# Revit family: Spec Equip_Shelf_Shower_Argent_Mondrian Neu_800mm
name_source: partatom
category: Specialty Equipment
revit_build: Autodesk Revit 2016 (Build: 20190508_0715(x64)
units: mm (PartAtom-declared; Revit-internal decimal feet)

## family parameters
Always vertical = Yes
Cut with Voids When Loaded = Yes
OmniClass Number = 23.40.20.21
OmniClass Title = Toilet and Bath Specialties
Part Type = Normal
Room Calculation Point = No
Round Connector Dimension = Use Diameter
Shared = No
Work Plane-Based = No

## types (1)
- Chrome (AR93611D)
    Body Material = z_Argent_Chrome
    CW Connection = No
    CWFU = 0
    Cost = 0 $
    Description = Mondrian Neu 300 Shower Shelf
    HW Connection = No
    HWFU = 0
    IfcExportAs = IfcSanitaryTerminalType
    IfcExportType = SHELF
    Manufacturer = Argent
    Manufacturer_Overall Depth = 100 mm
    Manufacturer_Overall Height = 25 mm
    Manufacturer_Overall Width = 300 mm
    Manufacturer_Spec Code = AR93611D
    Manufacturer_URL__Product Specific = https://www.argentaust.com.au
    Model = AR93611D
    ModifiedIssue_ANZRS = 20191125 $
    Type Comments = Chrome Finish
    URL = https://www.argentaust.com.au
    Uniclass2015Code = Pr_40_30_78_06
    Uniclass2015Title = Bathroom shelves
    Uniclass2015Version = Products v1.9
    Vent Connection = No
    WFU = 0
    Waste Connection = No

## geometry (parser evidence)
native form markers: Sweep x2
no freeform markers — native parametric forms only
